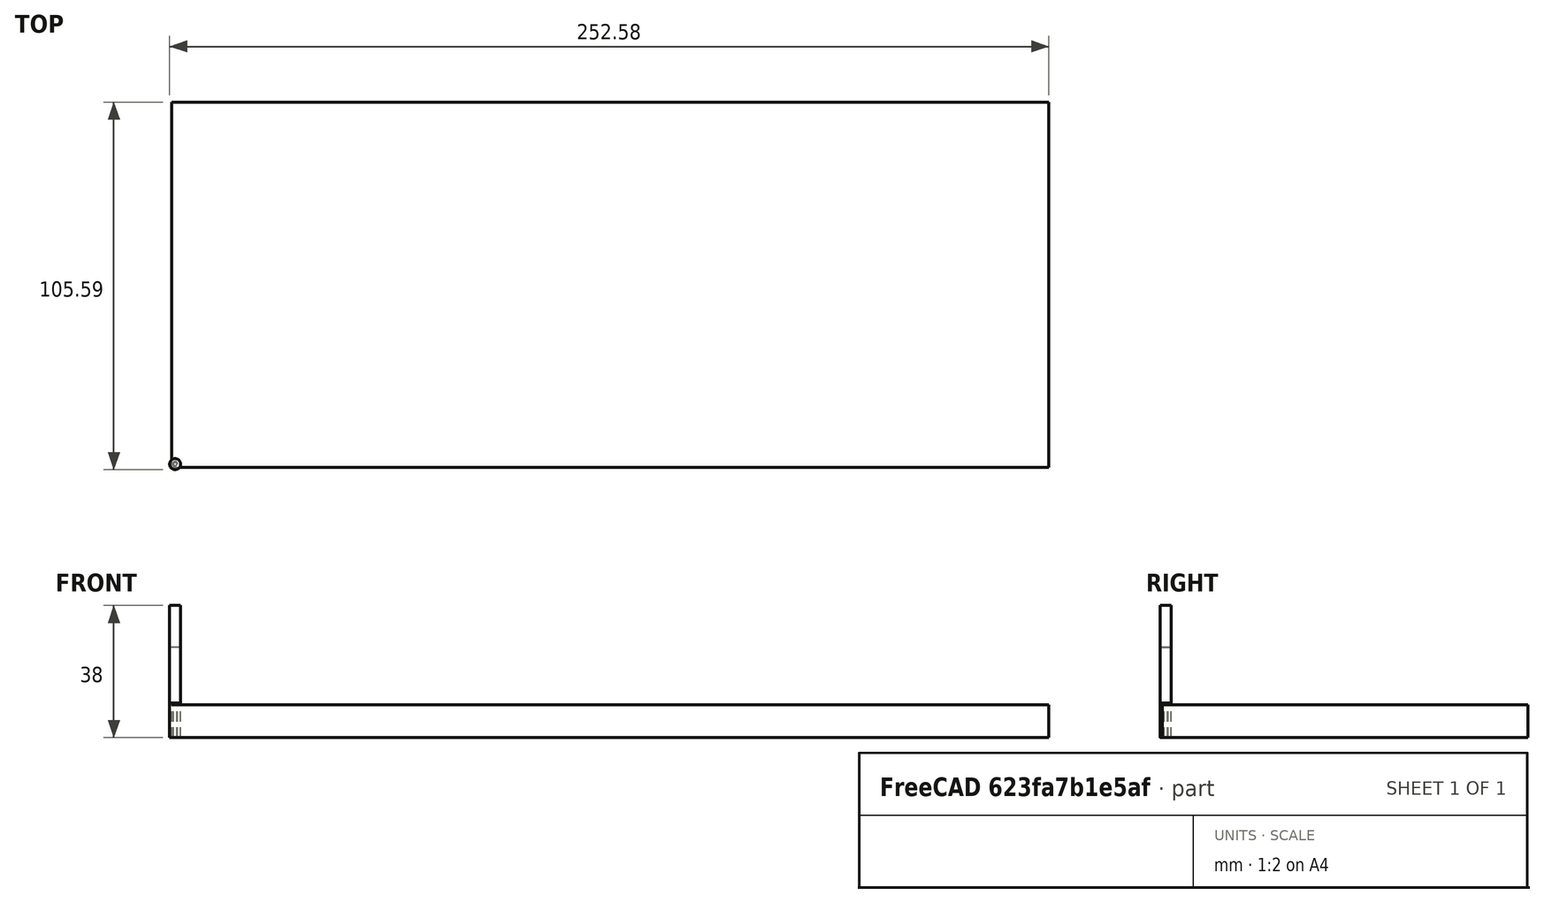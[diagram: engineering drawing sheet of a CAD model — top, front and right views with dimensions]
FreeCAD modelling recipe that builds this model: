
FCSTD DOCUMENT  (FreeCAD 0.21R33694 (Git))
Label: OIPTv2
License: Creative Commons Attribution 4.0
LicenseURL: https://creativecommons.org/licenses/by/4.0/
objects: Part::FeaturePython×5, Path::FeaturePython×5, Part::Part2DObjectPython×4, Part::Extrusion×4, App::DocumentObjectGroup×3, PartDesign::AdditiveBox×1, PartDesign::Body×1, Spreadsheet::Sheet×1, Part::MultiFuse×1, App::FeaturePython×1
note: 18 computed .brp shape members not serialized (recipe doc carries the construction recipe); baked Part::Feature solids carry a one-line shape summary decoded from their .brp

FEATURE [PartDesign::AdditiveBox] Box
  AttacherType = Attacher::AttachEngine3D
  Height = 9.3
  Length = 250
  MapMode = 5
  Support = -> [XY_Plane]
  Width = 103
  expr: Height = <<vars>>.height
  expr: Length = <<vars>>.length
  expr: Width = <<vars>>.width
FEATURE [PartDesign::Body] Body
  Group = -> [Box]
  Origin = -> Origin
  Tip = -> Box
FEATURE [Part::Part2DObjectPython] ShapeString  # Draft 2D object (typed FeaturePython)
  FontFile = /Library/Fonts/Arial Unicode.ttf
  Fuse = false
  Justification = 1
  JustificationReference = 0
  KeepLeftMargin = false
  MakeFace = true
  ObliqueAngle = 0
  Placement = pos=(43.8,77,9.4) rot=(0,0,1;0rad)
  ScaleToSize = true
  Size = 23
  String = ON-PREMISE
  Tracking = 0
  expr: .Placement.Base.y = <<vars>>.width - <<vars>>.border - <<vars>>.font_size
  expr: .Placement.Base.z = <<vars>>.height + 0.1
  expr: Size = <<vars>>.font_size
FEATURE [Part::Part2DObjectPython] ShapeString001  # Draft 2D object (typed FeaturePython)
  FontFile = /Library/Fonts/Arial Unicode.ttf
  Fuse = false
  Justification = 1
  JustificationReference = 0
  KeepLeftMargin = false
  MakeFace = true
  ObliqueAngle = 0
  Placement = pos=(6.5,54,9.4) rot=(0,0,1;0rad)
  ScaleToSize = true
  Size = 23
  String = INFRASTRUCTURE
  Tracking = 0
  expr: .Placement.Base.y = <<vars>>.width - <<vars>>.border - <<vars>>.font_size * 2
  expr: .Placement.Base.z = <<vars>>.height + 0.1
  expr: Size = <<vars>>.font_size
FEATURE [Part::Part2DObjectPython] ShapeString002  # Draft 2D object (typed FeaturePython)
  FontFile = /Library/Fonts/Arial Unicode.ttf
  Fuse = false
  Justification = 1
  JustificationReference = 0
  KeepLeftMargin = false
  MakeFace = true
  ObliqueAngle = 0
  Placement = pos=(52.45,31,9.4) rot=(0,0,1;0rad)
  ScaleToSize = true
  Size = 23
  String = PRODUCTS
  Tracking = 0
  expr: .Placement.Base.y = <<vars>>.width - <<vars>>.border - <<vars>>.font_size * 3
  expr: .Placement.Base.z = <<vars>>.height + 0.1
  expr: Size = <<vars>>.font_size
FEATURE [Spreadsheet::Sheet] Spreadsheet  label="vars"
  cells = A1='length; B1(length)=250; A2='width; B2(width)=103; C2==B2 + B2 / 4; A3='height; B3(height)=9.3; A4='cut_height; B4(cut_height)=2; A5='border; B5(border)=3; A6='font-size; B6(font_size)=23
FEATURE [Part::Part2DObjectPython] ShapeString003  # Draft 2D object (typed FeaturePython)
  FontFile = /Library/Fonts/Arial Unicode.ttf
  MakeFace = true
  Placement = pos=(90,8,9.4) rot=(2e-06,-2e-06,-1;2.9e-05rad)
  Size = 23
  String = TEAM
  Tracking = 0
  expr: .Placement.Base.y = <<vars>>.width - <<vars>>.border - <<vars>>.font_size * 4
  expr: .Placement.Base.z = <<vars>>.height + 0.1
  expr: Size = <<vars>>.font_size
FEATURE [Part::Extrusion] Extrude
  Base = -> ShapeString
  Dir = (0,0,1)
  DirMode = 2
  FaceMakerClass = Part::FaceMakerBullseye
  LengthFwd = 2
  LengthRev = 0
  Reversed = true
  Solid = false
  Symmetric = false
  expr: LengthFwd = <<vars>>.cut_height
FEATURE [Part::Extrusion] Extrude001
  Base = -> ShapeString001
  Dir = (0,0,1)
  DirMode = 2
  FaceMakerClass = Part::FaceMakerBullseye
  LengthFwd = 2
  LengthRev = 0
  Reversed = true
  Solid = false
  Symmetric = false
  expr: LengthFwd = <<vars>>.cut_height
FEATURE [Part::Extrusion] Extrude002
  Base = -> ShapeString002
  Dir = (0,0,1)
  DirMode = 2
  FaceMakerClass = Part::FaceMakerBullseye
  LengthFwd = 2
  LengthRev = 0
  Reversed = true
  Solid = false
  Symmetric = false
  expr: LengthFwd = <<vars>>.cut_height
FEATURE [Part::Extrusion] Extrude003
  Base = -> ShapeString003
  Dir = (-4.85269e-11,-6.44486e-11,1)
  DirMode = 2
  FaceMakerClass = Part::FaceMakerBullseye
  LengthFwd = 2
  LengthRev = 0
  Reversed = true
  Solid = false
  Symmetric = false
  expr: LengthFwd = <<vars>>.cut_height
FEATURE [Part::MultiFuse] Fusion
  Shapes = -> [Body,Extrude,Extrude001,Extrude002,Extrude003]
FEATURE [App::FeaturePython] SetupSheet  # Path/CAM operation (typed FeaturePython)
  ClearanceHeightExpression = OpStockZMax+SetupSheet.ClearanceHeightOffset
  ClearanceHeightOffset = 5
  CoolantMode = 0
  CoolantModes = None | Flood | Mist
  FinalDepthExpression = OpFinalDepth
  HorizRapid = 0
  SafeHeightExpression = OpStockZMax+SetupSheet.SafeHeightOffset
  SafeHeightOffset = 3
  StartDepthExpression = OpStartDepth
  StepDownExpression = OpToolDiameter
  VertRapid = 0
FEATURE [Part::FeaturePython] Clone  label="Model-Fusion"  # Draft clone (typed FeaturePython)
  AttacherType = Attacher::AttachEngine3D
  Fuse = false
  Objects = -> [Fusion]
  PathResource = Model
  Scale = (1,1,1)
FEATURE [App::DocumentObjectGroup] Model
  Group = -> [Clone]
FEATURE [Part::FeaturePython] ToolBit  label="1.0mm-endmill"  # Path/CAM toolbit (typed FeaturePython)
  BitPropertyNames = Chipload | CuttingEdgeHeight | Diameter | Flutes | Length | Material | ShankDiameter | SpindleDirection
  BitShape = /Applications/FreeCAD.app/Contents/Resources/Mod/Path/Tools/Shape/endmill.fcstd
  Chipload = 0
  CuttingEdgeHeight = 10
  Diameter = 1
  Flutes = 0
  Length = 38
  Material = 0
  ShankDiameter = 3.17
  ShapeName = endmill
  SpindleDirection = 0
FEATURE [Path::FeaturePython] __0mm_endmill  label="1.0mm-endmill001"  # Path/CAM operation (typed FeaturePython)
  HorizFeed = 16.6667
  HorizRapid = 0
  SpindleDir = 0
  SpindleSpeed = 5000
  Tool = -> ToolBit
  ToolNumber = 5
  VertFeed = 16.6667
  VertRapid = 0
  expr: HorizRapid = SetupSheet.HorizRapid
  expr: VertRapid = SetupSheet.VertRapid
FEATURE [Part::FeaturePython] ToolBit001  label="1.4mm-endmill"  # Path/CAM toolbit (typed FeaturePython)
  BitPropertyNames = Chipload | CuttingEdgeHeight | Diameter | Flutes | Length | Material | ShankDiameter | SpindleDirection
  BitShape = /Applications/FreeCAD.app/Contents/Resources/Mod/Path/Tools/Shape/endmill.fcstd
  Chipload = 0
  CuttingEdgeHeight = 10
  Diameter = 1.4
  Flutes = 0
  Length = 26
  Material = 0
  ShankDiameter = 3
  ShapeName = endmill
  SpindleDirection = 0
FEATURE [Path::FeaturePython] __4mm_endmill  label="1.4mm-endmill001"  # Path/CAM operation (typed FeaturePython)
  HorizFeed = 16.6667
  HorizRapid = 0
  SpindleDir = 0
  SpindleSpeed = 10000
  Tool = -> ToolBit001
  ToolNumber = 2
  VertFeed = 16.6667
  VertRapid = 0
  expr: HorizRapid = SetupSheet.HorizRapid
  expr: VertRapid = SetupSheet.VertRapid
FEATURE [Part::FeaturePython] ToolBit002  label="3.175mm-endmill"  # Path/CAM toolbit (typed FeaturePython)
  BitPropertyNames = Chipload | CuttingEdgeHeight | Diameter | Flutes | Length | Material | ShankDiameter | SpindleDirection
  BitShape = /Applications/FreeCAD.app/Contents/Resources/Mod/Path/Tools/Shape/endmill.fcstd
  Chipload = 0
  CuttingEdgeHeight = 10
  Diameter = 3.17
  Flutes = 0
  Length = 26
  Material = 0
  ShankDiameter = 3
  ShapeName = endmill
  SpindleDirection = 0
FEATURE [Path::FeaturePython] __175mm_endmill  label="3.175mm-endmill001"  # Path/CAM operation (typed FeaturePython)
  HorizFeed = 33.3333
  HorizRapid = 0
  SpindleDir = 0
  SpindleSpeed = 10000
  Tool = -> ToolBit002
  ToolNumber = 4
  VertFeed = 33.3333
  VertRapid = 0
  expr: HorizRapid = SetupSheet.HorizRapid
  expr: VertRapid = SetupSheet.VertRapid
FEATURE [App::DocumentObjectGroup] Tools
  Group = -> [__0mm_endmill,__4mm_endmill,__175mm_endmill]
FEATURE [Part::FeaturePython] Stock  # WARN: FeaturePython — macro-defined, semantics opaque (R4)
  Base = -> Model
  ExtXneg = 1
  ExtXpos = 1
  ExtYneg = 1
  ExtYpos = 1
  ExtZneg = 0
  ExtZpos = 0
  StockType = FromBase
FEATURE [Path::FeaturePython] Pocket_Shape  # Path/CAM operation (typed FeaturePython)
  Active = true
  AreaParams:
    Tolerance = 1e-07
    FitArcs = True
    Simplify = False
    CleanDistance = 0.0
    Accuracy = 0.01
    Unit = 1.0
    MinArcPoints = 4
    MaxArcPoints = 100
    ClipperScale = 10000000.0
    Fill = 0
    Coplanar = 0
    Reorient = True
    Outline = False
    Explode = False
    OpenMode = 0
    Deflection = 0.01
    SubjectFill = 0
    ClipFill = 0
    Offset = 0.0
    ExtraPass = 0
    Stepover = 0.0
    LastStepover = 0.0
    JoinType = 0
    EndType = 0
    MiterLimit = 2.0
    RoundPrecision = 0.0
    PocketMode = 2
    ToolRadius = 0.5
    PocketExtraOffset = 0.0
    PocketStepover = 1.0
    PocketLastStepover = 0.0
    FromCenter = True
    Angle = 45.0
    AngleShift = 0.0
    Shift = 0.0
    Thicken = False
    SectionCount = -1
    Stepdown = 1.0
    SectionOffset = 0.0
    SectionTolerance = 1e-07
    SectionMode = 2
    Project = False
  Base = -> [Clone]
  ClearanceHeight = 14.4
  CoolantMode = 0
  CutMode = 0
  CycleTime = 01:03:20
  ExtensionCorners = true
  ExtensionLengthDefault = 0.5
  ExtraOffset = 0
  FinalDepth = 7.3
  FinishDepth = 0
  KeepToolDown = false
  MinTravel = false
  OffsetPattern = 1
  OpFinalDepth = 9.4
  OpStartDepth = 9.73333
  OpStockZMax = 9.4
  OpStockZMin = 0
  OpToolDiameter = 1
  PathParams = {'orientation': 1, 'feedrate': 16.666666666666668, 'feedrate_v': 16.666666666666668, 'verbose': True, 'resume_height': 12.400000004563674, 'retraction': 14.400000004563674, 'return_end': True, 'preamble': False, 'start': Vector (142.88801015364433, 45.46693010372361, 14.400000004563674)}
  PocketLastStepOver = 0
  SafeHeight = 12.4
  SplitArcs = false
  StartAt = 0
  StartDepth = 9.3
  StartPoint = (0,0,0)
  StepDown = 0.333333
  StepOver = 100
  ToolController = -> __0mm_endmill
  UseOutline = false
  UseStartPoint = false
  ZigZagAngle = 45
  expr: ClearanceHeight = OpStockZMax + SetupSheet.ClearanceHeightOffset
  expr: ExtensionLengthDefault = OpToolDiameter / 2
  expr: FinalDepth = 7.3
  expr: SafeHeight = OpStockZMax + SetupSheet.SafeHeightOffset
  expr: StartDepth = 9.3
  expr: StepDown = OpToolDiameter / 3
FEATURE [App::DocumentObjectGroup] Operations
  Group = -> [Pocket_Shape]
FEATURE [Path::FeaturePython] Job  # Path/CAM operation (typed FeaturePython)
  CycleTime = 01:03:20
  Fixtures = G54
  GeometryTolerance = 0.01
  JobType = 0
  LastPostProcessDate = 2024-02-25 13:00:10.346875
  LastPostProcessOutput = /Volumes/NEW VOLUME/oipt.nc
  Model = -> Model
  Operations = -> Operations
  OrderOutputBy = 0
  PostProcessor = 1
  PostProcessorOutputFile = <userpath>/3d_projects/CNC-stuff/placard/nameplate.nc
  SetupSheet = -> SetupSheet
  SplitOutput = false
  Stock = -> Stock
  Tools = -> Tools
